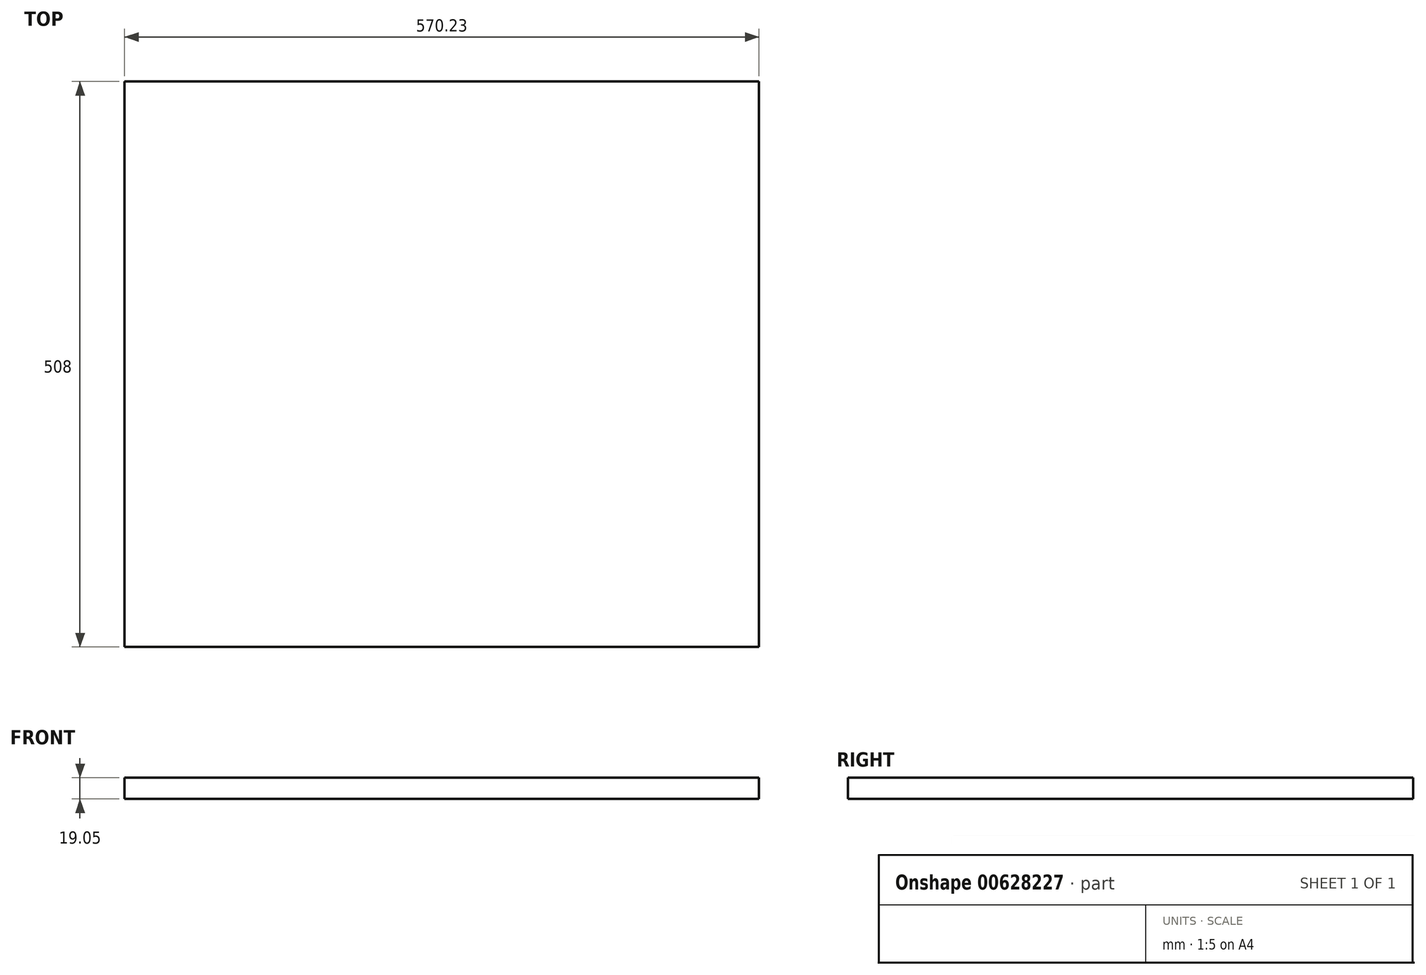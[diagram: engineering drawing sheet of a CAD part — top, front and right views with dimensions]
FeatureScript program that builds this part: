
annotation { "Feature Type Name" : "Feature", "Feature Type Description" : "" }
export const myFeature = defineFeature(function(context is Context, id is Id, definition is map)
    precondition{}
    {
        {
            var Q0;
            Q0=qCreatedBy(makeId("Top.planeOp"),FACE);
            var sketch = newSketch(context, id + "F0", { "sketchPlane" : qUnion([Q0])});
            skLineSegment(sketch, "E0.bottom", {"start": v(0, 0) * mm, "end": v(570.23, 0) * mm});
            skLineSegment(sketch, "E0.top", {"start": v(0, 508) * mm, "end": v(570.23, 508) * mm});
            skLineSegment(sketch, "E0.left", {"start": v(0, 0) * mm, "end": v(0, 508) * mm});
            skLineSegment(sketch, "E0.right", {"start": v(570.23, 0) * mm, "end": v(570.23, 508) * mm});
            skSolve(sketch);
        }
        {
            var Q0;
            Q0=makeQuery(id+"F0.imprint","IMPRINT",FACE,{"disambiguationData":[TD([[makeQuery(id+"F0.imprint","IMPRINT",EDGE,{"derivedFrom":sQuery(id+"F0.wireOp",EDGE,"E0.bottom")}),1.0]])]});
            extrude(context, id + "F1", {"entities" : qUnion([Q0]), "depth" : 19.05 * mm, "offsetDistance" : 25.4 * mm});
        }
    });
